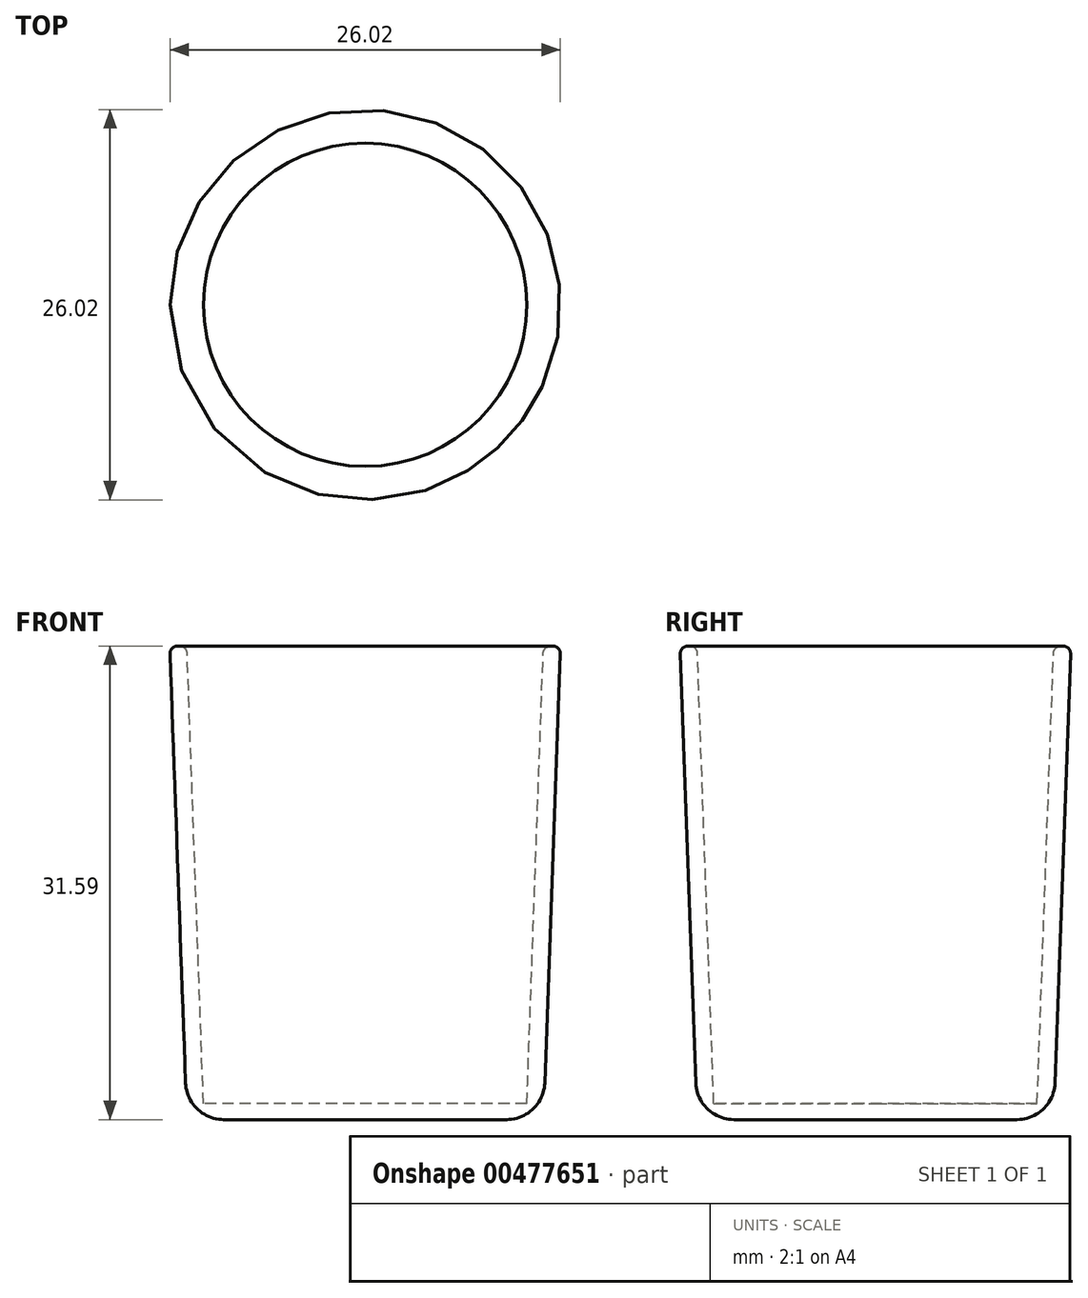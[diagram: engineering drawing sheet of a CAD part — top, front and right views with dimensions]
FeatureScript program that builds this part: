
annotation { "Feature Type Name" : "Feature", "Feature Type Description" : "" }
export const myFeature = defineFeature(function(context is Context, id is Id, definition is map)
    precondition{}
    {
        {
            var Q0;
            Q0=qCreatedBy(makeId("Front.planeOp"),FACE);
            var sketch = newSketch(context, id + "F0", { "sketchPlane" : qUnion([Q0])});
            skLineSegment(sketch, "E0", {"start": v(0, 0) * mm, "end": v(11.89, 0) * mm});
            skLineSegment(sketch, "E1", {"start": v(11.89, 0) * mm, "end": v(13.03, 31.59) * mm});
            skLineSegment(sketch, "E2", {"start": v(13.03, 31.59) * mm, "end": v(11.89, 31.59) * mm});
            skLineSegment(sketch, "E3", {"start": v(11.89, 31.59) * mm, "end": v(10.78, 1.05) * mm});
            skLineSegment(sketch, "E4", {"start": v(10.78, 1.05) * mm, "end": v(0, 1.05) * mm});
            skLineSegment(sketch, "E5", {"start": v(0, 1.05) * mm, "end": v(0, 0) * mm});
            skSolve(sketch);
        }
        {
            var Q0;
            Q0 = qSketchRegion(id + "F0", true);
            var Q1;
            Q1=sQuery(id+"F0.wireOp",EDGE,"E5");
            revolve(context, id + "F1", {"entities" : qUnion([Q0]), "axis" : qUnion([Q1]), "revolveType" : RevolveType.FULL});
        }
        {
            var Q0;
            Q0=makeQuery(id+"F1.opRevolve","SWEPT_EDGE",EDGE,{"disambiguationData":[OSD([sQuery(id+"F0.wireOp",EDGE,"E2"),sQuery(id+"F0.wireOp",EDGE,"E3")])]});
            var Q1;
            Q1=makeQuery(id+"F1.opRevolve","SWEPT_EDGE",EDGE,{"disambiguationData":[OSD([sQuery(id+"F0.wireOp",EDGE,"E1"),sQuery(id+"F0.wireOp",EDGE,"E2")])]});
            fillet(context, id + "F2", {"entities" : qUnion([Q0, Q1]), "radius" : 0.5 * mm, "tangentPropagation" : true, "allowEdgeOverflow" : false});
        }
        {
            var Q0;
            Q0=makeQuery(id+"F1.opRevolve","SWEPT_EDGE",EDGE,{"disambiguationData":[OSD([sQuery(id+"F0.wireOp",EDGE,"E0"),sQuery(id+"F0.wireOp",EDGE,"E1")])]});
            fillet(context, id + "F3", {"entities" : qUnion([Q0]), "radius" : 2.54 * mm, "tangentPropagation" : true, "allowEdgeOverflow" : false});
        }
    });
